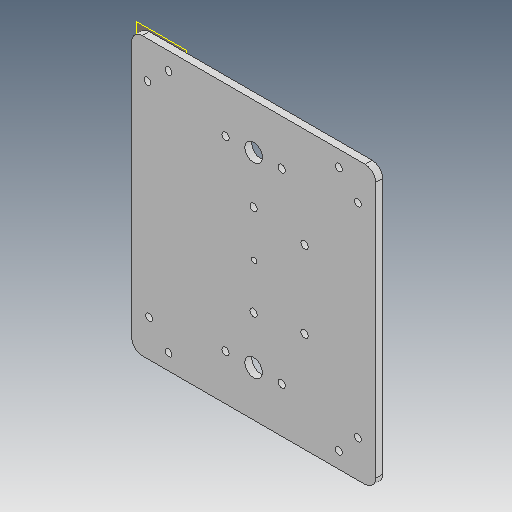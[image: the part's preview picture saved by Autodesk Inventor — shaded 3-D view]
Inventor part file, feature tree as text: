
AUTODESK INVENTOR PART (.ipt)
format: ipt  version: 2020 (Build 240168000, 168)  size: 187,392 bytes
history: native  units: mm
features: other x23, extrude x5, sketch x5
ambient origin geometry x8: Origin, YZ Plane, XZ Plane, XY Plane, X Axis, Y Axis, Z Axis, Center Point
bodies: Body1 (feature_tree)
feature tree (33):
  other  "Sólido1"
  other  "Plano de trabalho1"
  extrude  "Extrusão1"  Depth=10.1mm
  extrude  "Extrusão2"  Depth=3.0mm
  extrude  "Extrusão3"  Depth=4.0mm
  extrude  "Extrusão4"  Depth=4.2mm
  extrude  "Extrusão5"  Depth=10.0mm
  sketch  "Esboço1"  dims[d1=0.0mm d2=10.1mm]
  other  "Referência1"
  other  "Referência2"
  other  "Referência3"
  other  "Referência4"
  sketch  "Esboço2"  dims[d3=4.2mm d4=3.0mm]
  other  "Referência5"
  other  "Referência6"
  other  "Referência7"
  other  "Referência8"
  other  "Referência9"
  sketch  "Esboço3"  dims[d5=4.0mm d6=0.0mm d7=32.0mm]
  sketch  "Esboço4"  dims[d8=32.0mm d9=4.2mm]
  sketch  "Esboço5"  dims[d10=4.2mm d11=4.2mm d12=4.2mm d13=4.0mm d14=0.0mm d15=4.2mm d16=4.2mm d17=4.0mm d18=0.0mm d19=10.0mm d20=10.1mm d21=10.1mm d22=10.0mm d23=0.0mm]
  other  "Calorímetro.iam"
  other  "suporte_fechamento:1"
  other  "suporte_fechamento:2"
  other  "<userpath>\OneDrive\Área de Trabalho\Calorimetro 2022\Inventor\Calorímetro.iam"
  other  "suporte_fechamento2:2"
  other  "suporte_fechamento2:3"
  other  "parte_superior:1"
  other  "guia_10mm:1"
  other  "guia_10mm:2"
  other  "Montagem_corpo_menor:1"
  other  "corpo_1_menor:4"
  other  "Inferior_encaixe:1"
